# Revit family: Tissue_Holder-DXV-Fitzgerald-D35160230_Series
name_source: partatom
category: Specialty Equipment
units: mm (PartAtom-declared; Revit-internal decimal feet)

## family parameters
Cut with Voids When Loaded = No
Host = Face
OmniClass Number = 23.40.20.21.21
OmniClass Title = Toilet Paper Dispensers
Part Type = Normal
Room Calculation Point = No
Round Connector Dimension = Use Diameter
Shared = Yes

## types (3) — shared parameters
ADA Compliant = Yes
Assembly Code = C1030220
Default Elevation = 25"
Description = Fitzgerald Toilet Paper Holder
Height = 4"
Installation Type = Wall Mounted
Length = 8 1/2"
Manufacturer = DXV
Price = Prices may vary. Please consult Manufacturer Representative for most up-to-date price list.
Product Documentation Link = https://dxv01.blob.core.windows.net
Product Page URL = https://www.dxv.com
Revised Date = 11/17/2021
Shipping Weight = 0 lb
URL = http://www.dxv.com
Warranty Information = Lifetime Limited Warranty
Width = 2"

## per-type parameters (varying)
| type | Finish | Material |
| D35160230.100 | Brass-DXV-100-Polished Chrome | Brass-DXV-100-Polished Chrome |
| D35160230.144 | Brass-DXV-144-Brushed Nickel | Brass-DXV-144-Brushed Nickel |
| D35160230.150 | Brass-DXV-150-Platinum Nickel | Brass-DXV-150-Platinum Nickel |

note: column(s) folded — value = type name in every type: Model

## geometry (parser evidence)
native form markers: Sweep x3
no freeform markers — native parametric forms only
